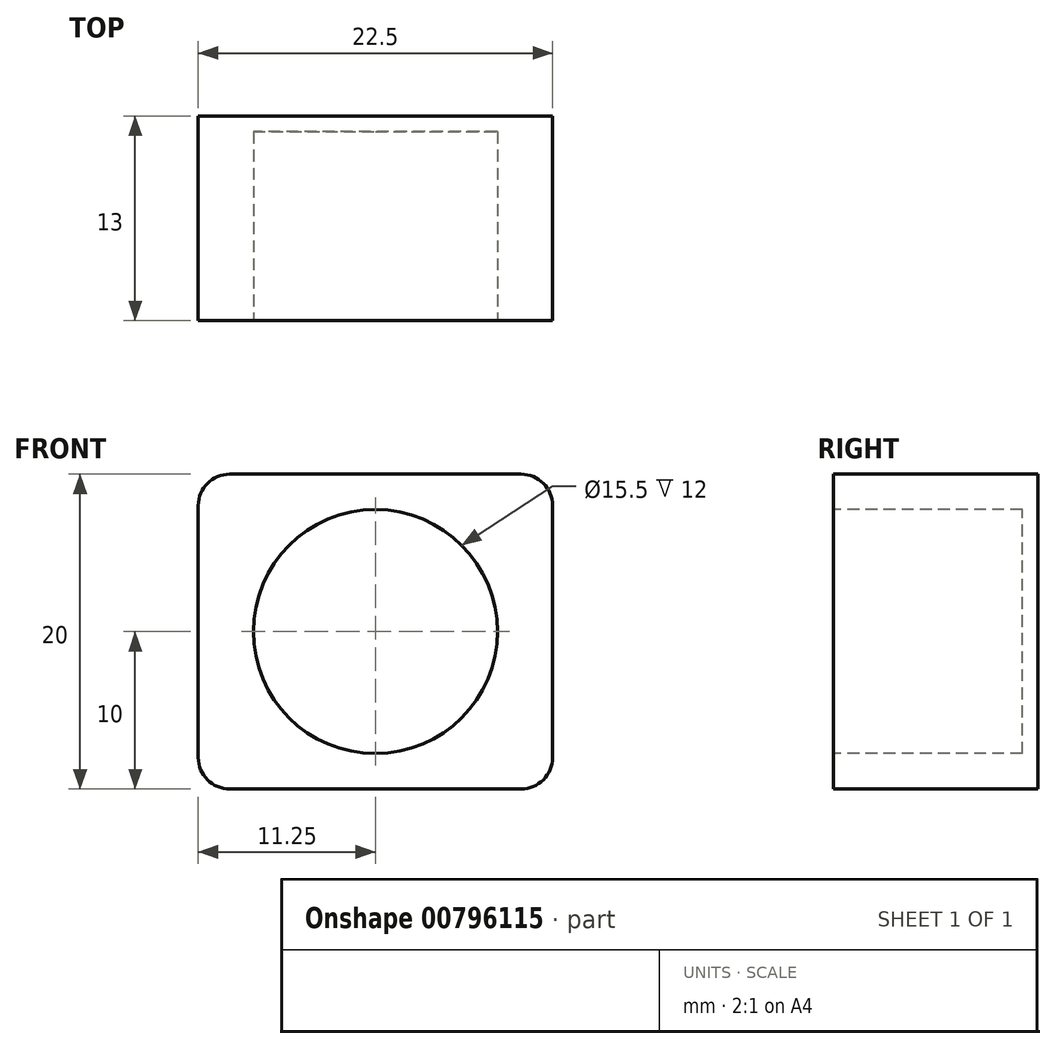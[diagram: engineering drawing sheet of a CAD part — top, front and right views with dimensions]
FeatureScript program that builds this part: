
annotation { "Feature Type Name" : "Feature", "Feature Type Description" : "" }
export const myFeature = defineFeature(function(context is Context, id is Id, definition is map)
    precondition{}
    {
        {
            var Q0;
            Q0=qCreatedBy(makeId("Top.planeOp"),FACE);
            var sketch = newSketch(context, id + "F0", { "sketchPlane" : qUnion([Q0])});
            skLineSegment(sketch, "E0", {"start": v(0, 0) * mm, "end": v(0, 13) * mm});
            skLineSegment(sketch, "E1", {"start": v(0, 13) * mm, "end": v(22.5, 13) * mm});
            skLineSegment(sketch, "E2", {"start": v(22.5, 13) * mm, "end": v(22.5, 0) * mm});
            skLineSegment(sketch, "E3", {"start": v(22.5, 0) * mm, "end": v(0, 0) * mm});
            skSolve(sketch);
        }
        {
            var Q0;
            Q0=makeQuery(id+"F0.imprint","IMPRINT",FACE,{"disambiguationData":[TD([[makeQuery(id+"F0.imprint","IMPRINT",EDGE,{"derivedFrom":sQuery(id+"F0.wireOp",EDGE,"E0")}),-1.0]])]});
            extrude(context, id + "F1", {"entities" : qUnion([Q0]), "depth" : 20 * mm, "offsetDistance" : 25 * mm});
        }
        {
            var Q0;
            Q0=makeQuery(id+"F1.opExtrude","SWEPT_FACE",FACE,{"disambiguationData":[OSD([sQuery(id+"F0.wireOp",EDGE,"E3")])]});
            var sketch = newSketch(context, id + "F2", { "sketchPlane" : qUnion([Q0])});
            skLineSegment(sketch, "E4", {"start": v(0, 0) * mm, "end": v(22.5, 20) * mm, "construction": true});
            skLineSegment(sketch, "E5", {"start": v(22.5, 20) * mm, "end": v(22.5, 0) * mm, "construction": true});
            skLineSegment(sketch, "E6", {"start": v(22.5, 0) * mm, "end": v(0, 20) * mm, "construction": true});
            skLineSegment(sketch, "E7", {"start": v(0, 20) * mm, "end": v(11.25, 10) * mm, "construction": true});
            skLineSegment(sketch, "E8", {"start": v(11.25, 10) * mm, "end": v(11.25, 20) * mm, "construction": true});
            skLineSegment(sketch, "E9", {"start": v(11.25, 20) * mm, "end": v(22.5, 10) * mm, "construction": true});
            skLineSegment(sketch, "E10", {"start": v(22.5, 10) * mm, "end": v(11.25, 0) * mm, "construction": true});
            skLineSegment(sketch, "E11", {"start": v(11.25, 0) * mm, "end": v(11.25, 10) * mm, "construction": true});
            skLineSegment(sketch, "E12", {"start": v(11.25, 10) * mm, "end": v(0, 10) * mm, "construction": true});
            skLineSegment(sketch, "E13", {"start": v(0, 10) * mm, "end": v(11.25, 20) * mm, "construction": true});
            skLineSegment(sketch, "E14", {"start": v(0, 10) * mm, "end": v(11.25, 0) * mm, "construction": true});
            skLineSegment(sketch, "E15", {"start": v(11.25, 10) * mm, "end": v(22.5, 10) * mm, "construction": true});
            skLineSegment(sketch, "E16", {"start": v(5.62, 15) * mm, "end": v(5.62, 5) * mm, "construction": true});
            skLineSegment(sketch, "E17", {"start": v(5.62, 5) * mm, "end": v(16.88, 5) * mm, "construction": true});
            skLineSegment(sketch, "E18", {"start": v(16.88, 5) * mm, "end": v(16.88, 15) * mm, "construction": true});
            skLineSegment(sketch, "E19", {"start": v(16.88, 15) * mm, "end": v(5.62, 15) * mm, "construction": true});
            skCircle(sketch, "E20", {"center": v(11.25, 10) * mm, "radius": 7.75 * mm});
            skSolve(sketch);
        }
        {
            var Q0;
            Q0=makeQuery(id+"F2.imprint","IMPRINT",FACE,{"disambiguationData":[TD([[makeQuery(id+"F2.imprint","IMPRINT",EDGE,{"derivedFrom":sQuery(id+"F2.wireOp",EDGE,"E20")}),1.0]])]});
            var Q1;
            Q1=sQuery(id+"F2.wireOp",EDGE,"E20");
            extrude(context, id + "F3", {"entities" : qUnion([Q0]), "operationType" : NewBodyOperationType.REMOVE, "surfaceOperationType" : NewSurfaceOperationType.ADD, "surfaceEntities" : qUnion([Q1]), "oppositeDirection" : true, "depth" : 12 * mm, "hasOffset" : true, "offsetDistance" : 12 * mm});
        }
        {
            var Q0;
            Q0=makeQuery(id+"F1.opExtrude","CAP_EDGE",EDGE,{"disambiguationData":[OSD([sQuery(id+"F0.wireOp",EDGE,"E2")])],"isStart":false});
            var Q1;
            Q1=makeQuery(id+"F1.opExtrude","CAP_EDGE",EDGE,{"disambiguationData":[OSD([sQuery(id+"F0.wireOp",EDGE,"E2")])],"isStart":true});
            var Q2;
            Q2=makeQuery(id+"F1.opExtrude","CAP_EDGE",EDGE,{"disambiguationData":[OSD([sQuery(id+"F0.wireOp",EDGE,"E0")])],"isStart":false});
            var Q3;
            Q3=makeQuery(id+"F1.opExtrude","CAP_EDGE",EDGE,{"disambiguationData":[OSD([sQuery(id+"F0.wireOp",EDGE,"E0")])],"isStart":true});
            fillet(context, id + "F4", {"entities" : qUnion([Q0, Q1, Q2, Q3]), "radius" : 2 * mm, "tangentPropagation" : true, "allowEdgeOverflow" : false});
        }
    });
